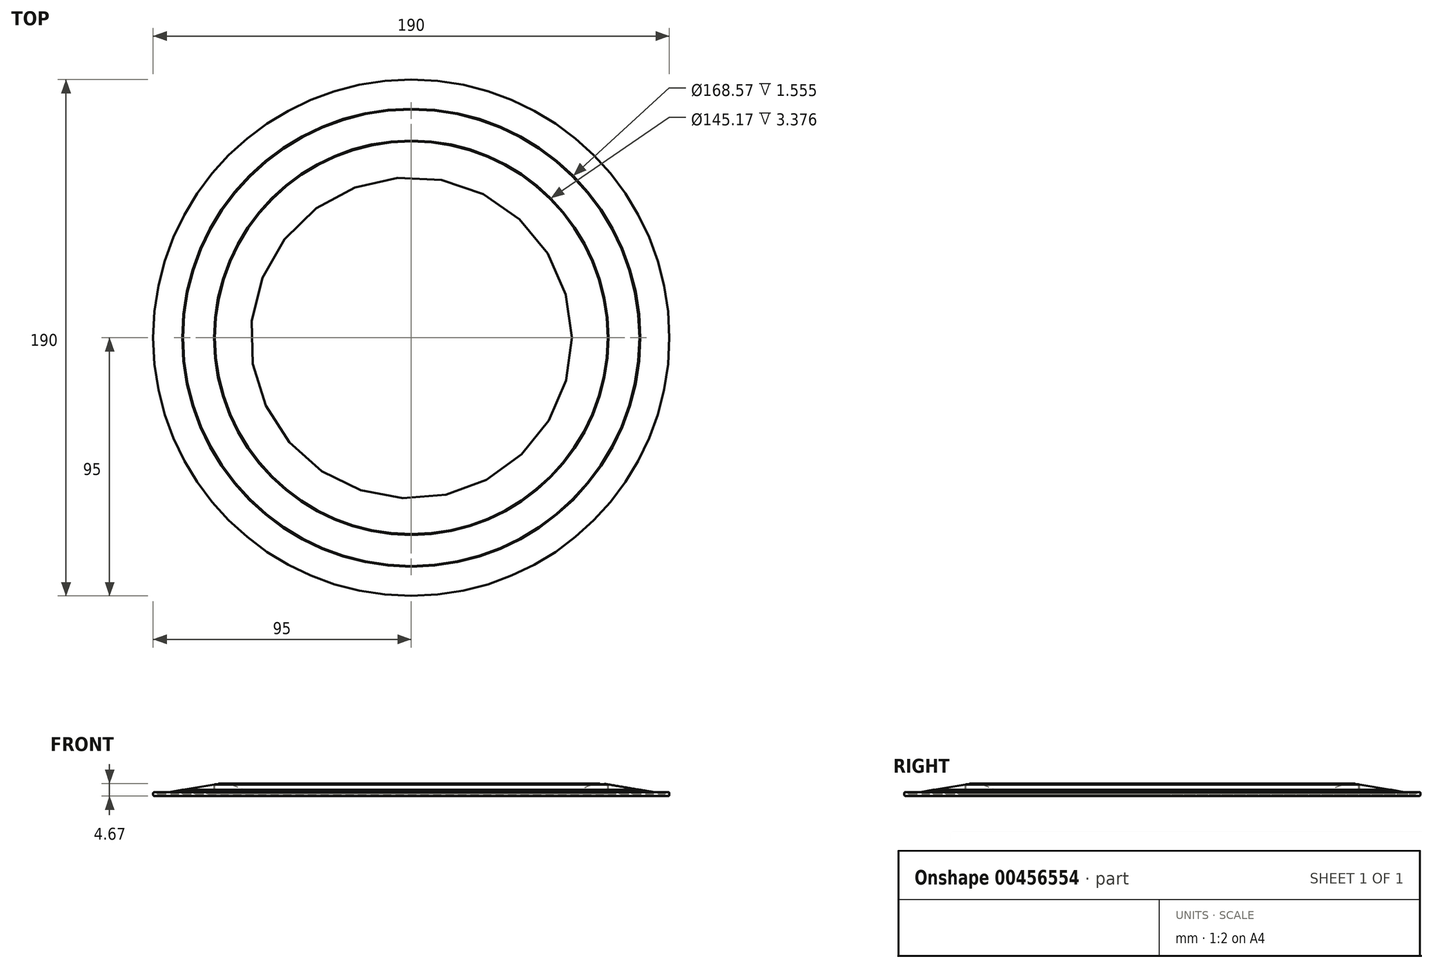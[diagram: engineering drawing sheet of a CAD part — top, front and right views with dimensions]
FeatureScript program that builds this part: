
annotation { "Feature Type Name" : "Feature", "Feature Type Description" : "" }
export const myFeature = defineFeature(function(context is Context, id is Id, definition is map)
    precondition{}
    {
        {
            var Q0;
            Q0=qCreatedBy(makeId("Top.planeOp"),FACE);
            var sketch = newSketch(context, id + "F0", { "sketchPlane" : qUnion([Q0])});
            skPoint(sketch, "E0.middle", {"position": v(0, 0) * mm});
            skCircle(sketch, "E1", {"center": v(0, 0) * mm, "radius": 95 * mm});
            skPoint(sketch, "E2.orphan", {"position": v(-95, 95) * mm});
            skPoint(sketch, "E0.right.end.orphan", {"position": v(-95, -95) * mm});
            skPoint(sketch, "E3.orphan", {"position": v(95, -95) * mm});
            skPoint(sketch, "E0.bottom.start.orphan", {"position": v(95, 95) * mm});
            skCircle(sketch, "E4.0", {"center": v(0, 0) * mm, "radius": 55 * mm});
            skSolve(sketch);
        }
        {
            var Q0;
            Q0=qCreatedBy(makeId("Front.planeOp"),FACE);
            var sketch = newSketch(context, id + "F1", { "sketchPlane" : qUnion([Q0])});
            skLineSegment(sketch, "E5", {"start": v(-56, 0) * mm, "end": v(-95, 0) * mm});
            skLineSegment(sketch, "E6", {"start": v(-68.29, 5) * mm, "end": v(-72.29, 4.33) * mm});
            skLineSegment(sketch, "E7", {"start": v(-95, 0.5) * mm, "end": v(-95, 0) * mm});
            skLineSegment(sketch, "E8", {"start": v(-56, 0) * mm, "end": v(-68.29, 5) * mm});
            skPoint(sketch, "E9.end.orphan", {"position": v(-65, 0) * mm});
            skLineSegment(sketch, "E10", {"start": v(-95, 0.5) * mm, "end": v(-95, 1.5) * mm});
            skLineSegment(sketch, "E11", {"start": v(-68.29, 5) * mm, "end": v(-68.29, 0) * mm, "construction": true});
            skLineSegment(sketch, "E12", {"start": v(-95, 1.5) * mm, "end": v(-93.75, 1.5) * mm});
            skLineSegment(sketch, "E13", {"start": v(-93.75, 1.5) * mm, "end": v(-93.5, 0.75) * mm});
            skLineSegment(sketch, "E14", {"start": v(-84.29, 2.3) * mm, "end": v(-84.29, 0.75) * mm});
            skLineSegment(sketch, "E15", {"start": v(-84.29, 0.75) * mm, "end": v(-72.29, 0.75) * mm});
            skLineSegment(sketch, "E16", {"start": v(-72.29, 0.75) * mm, "end": v(-72.29, 4.33) * mm});
            skLineSegment(sketch, "E17.trimOffspring", {"start": v(-84.29, 2.3) * mm, "end": v(-93.5, 0.75) * mm});
            skLineSegment(sketch, "E18", {"start": v(0, 94.77) * mm, "end": v(0, -67.17) * mm, "construction": true});
            skLineSegment(sketch, "E19.0", {"start": v(-72.59, 0.9) * mm, "end": v(-72.59, 4.28) * mm});
            skLineSegment(sketch, "E19.1", {"start": v(-83.99, 0.9) * mm, "end": v(-72.59, 0.9) * mm});
            skLineSegment(sketch, "E20", {"start": v(-83.99, 2.36) * mm, "end": v(-72.59, 4.28) * mm});
            skLineSegment(sketch, "E21", {"start": v(-83.99, 0.9) * mm, "end": v(-83.99, 2.36) * mm});
            skLineSegment(sketch, "E22", {"start": v(31.22, 145.17) * mm, "end": v(108.68, 67.12) * mm, "construction": true});
            skLineSegment(sketch, "E23", {"start": v(108.68, 67.12) * mm, "end": v(108.68, 0) * mm, "construction": true});
            skSolve(sketch);
        }
        {
            var Q0;
            Q0=makeQuery(id+"F1.imprint","IMPRINT",FACE,{"disambiguationData":[TD([[makeQuery(id+"F1.imprint","IMPRINT",EDGE,{"derivedFrom":sQuery(id+"F1.wireOp",EDGE,"E5")}),-1.0]])]});
            var Q1;
            Q1=sQuery(id+"F1.wireOp",EDGE,"E18");
            revolve(context, id + "F2", {"entities" : qUnion([Q0]), "axis" : qUnion([Q1]), "revolveType" : RevolveType.FULL});
        }
        {
            var Q0;
            Q0=makeQuery(id+"F2.opRevolve","SWEPT_EDGE",EDGE,{"disambiguationData":[OSD([sQuery(id+"F1.wireOp",EDGE,"E6"),sQuery(id+"F1.wireOp",EDGE,"E8")])]});
            fillet(context, id + "F3", {"entities" : qUnion([Q0]), "radius" : 10 * mm, "tangentPropagation" : true, "allowEdgeOverflow" : false});
        }
        {
            var Q0;
            Q0=makeQuery(id+"F2.opRevolve","SWEPT_EDGE",EDGE,{"disambiguationData":[OSD([sQuery(id+"F1.wireOp",EDGE,"E12"),sQuery(id+"F1.wireOp",EDGE,"E13")])]});
            var Q1;
            Q1=makeQuery(id+"F2.opRevolve","SWEPT_EDGE",EDGE,{"disambiguationData":[OSD([sQuery(id+"F1.wireOp",EDGE,"E10"),sQuery(id+"F1.wireOp",EDGE,"E12")])]});
            var Q2;
            Q2=makeQuery(id+"F2.opRevolve","SWEPT_EDGE",EDGE,{"disambiguationData":[OSD([sQuery(id+"F1.wireOp",EDGE,"E5"),sQuery(id+"F1.wireOp",EDGE,"E7")])]});
            fillet(context, id + "F4", {"entities" : qUnion([Q0, Q1, Q2]), "radius" : .5 * mm, "tangentPropagation" : true, "allowEdgeOverflow" : false});
        }
        {
            var Q0;
            Q0=makeQuery(id+"F2.opRevolve","SWEPT_EDGE",EDGE,{"disambiguationData":[OSD([sQuery(id+"F1.wireOp",EDGE,"E13"),sQuery(id+"F1.wireOp",EDGE,"E17.trimOffspring")])]});
            fillet(context, id + "F5", {"entities" : qUnion([Q0]), "radius" : .5 * mm, "tangentPropagation" : true, "allowEdgeOverflow" : false});
        }
        {
            var Q0;
            Q0=makeQuery(id+"F2.opRevolve","SWEPT_EDGE",EDGE,{"disambiguationData":[OSD([sQuery(id+"F1.wireOp",EDGE,"E5"),sQuery(id+"F1.wireOp",EDGE,"E8")])]});
            fillet(context, id + "F6", {"entities" : qUnion([Q0]), "radius" : .75 * mm, "tangentPropagation" : true, "allowEdgeOverflow" : false});
        }
        {
            var Q0;
            Q0=makeQuery(id+"F1.imprint","IMPRINT",FACE,{"disambiguationData":[TD([[makeQuery(id+"F1.imprint","IMPRINT",EDGE,{"derivedFrom":sQuery(id+"F1.wireOp",EDGE,"E19.0")}),1.0]])]});
            var Q1;
            Q1=sQuery(id+"F1.wireOp",EDGE,"E18");
            revolve(context, id + "F7", {"entities" : qUnion([Q0]), "axis" : qUnion([Q1]), "revolveType" : RevolveType.FULL});
        }
        {
            var Q0;
            Q0=qCreatedBy(makeId("Top.planeOp"),FACE);
            cPlane(context, id + "F8", {"entities" : qUnion([Q0]), "cplaneType" : CPlaneType.OFFSET, "offset" : 7 * mm, "width" : 150 * mm, "height" : 150 * mm});
        }
    });
